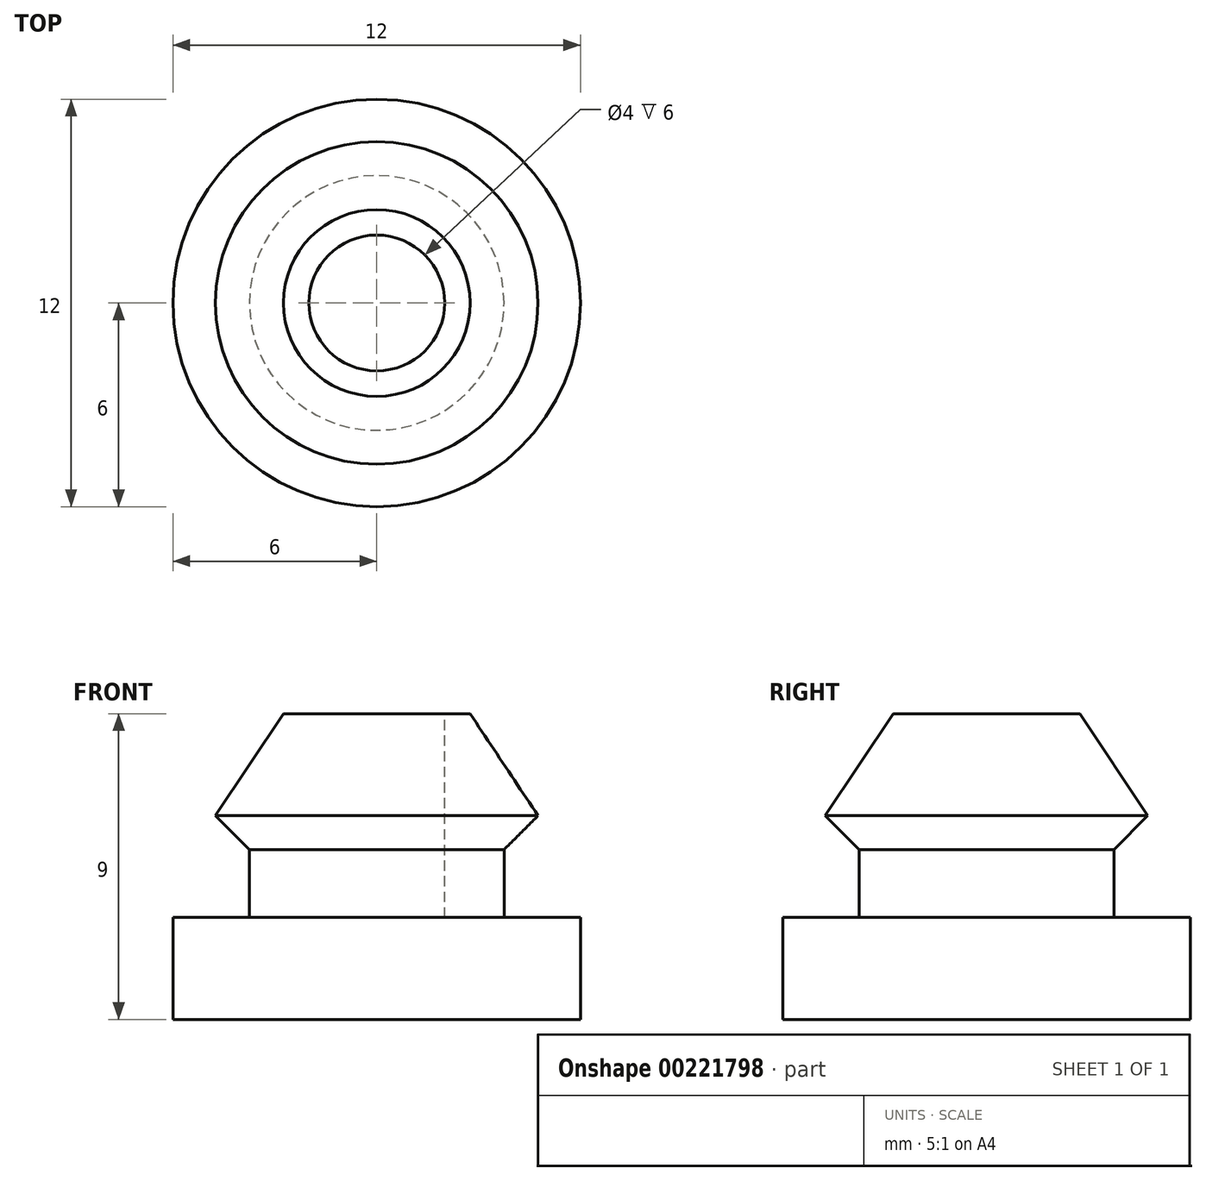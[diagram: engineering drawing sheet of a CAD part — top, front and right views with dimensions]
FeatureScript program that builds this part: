
annotation { "Feature Type Name" : "Feature", "Feature Type Description" : "" }
export const myFeature = defineFeature(function(context is Context, id is Id, definition is map)
    precondition{}
    {
        {
            var Q0;
            Q0=qCreatedBy(makeId("Front.planeOp"),FACE);
            var sketch = newSketch(context, id + "F0", { "sketchPlane" : qUnion([Q0])});
            skLineSegment(sketch, "E0", {"start": v(0, 0) * mm, "end": v(6, 0) * mm});
            skLineSegment(sketch, "E1", {"start": v(6, 0) * mm, "end": v(6, 3) * mm});
            skLineSegment(sketch, "E2", {"start": v(6, 3) * mm, "end": v(3.75, 3) * mm});
            skLineSegment(sketch, "E3", {"start": v(3.75, 3) * mm, "end": v(3.75, 5) * mm});
            skLineSegment(sketch, "E4", {"start": v(3.75, 5) * mm, "end": v(4.75, 6) * mm});
            skLineSegment(sketch, "E5", {"start": v(4.75, 6) * mm, "end": v(2.75, 9) * mm});
            skLineSegment(sketch, "E6", {"start": v(0, 3) * mm, "end": v(0, 0) * mm});
            skLineSegment(sketch, "E7", {"start": v(2.75, 9) * mm, "end": v(2, 9) * mm});
            skLineSegment(sketch, "E8", {"start": v(2, 9) * mm, "end": v(2, 3) * mm});
            skLineSegment(sketch, "E9", {"start": v(2, 3) * mm, "end": v(0, 3) * mm});
            skSolve(sketch);
        }
        {
            var Q0;
            Q0=makeQuery(id+"F0.imprint","IMPRINT",FACE,{"disambiguationData":[TD([[makeQuery(id+"F0.imprint","IMPRINT",EDGE,{"derivedFrom":sQuery(id+"F0.wireOp",EDGE,"E0")}),1.0]])]});
            var Q1;
            Q1=sQuery(id+"F0.wireOp",EDGE,"E6");
            revolve(context, id + "F1", {"entities" : qUnion([Q0]), "axis" : qUnion([Q1]), "revolveType" : RevolveType.FULL});
        }
    });
